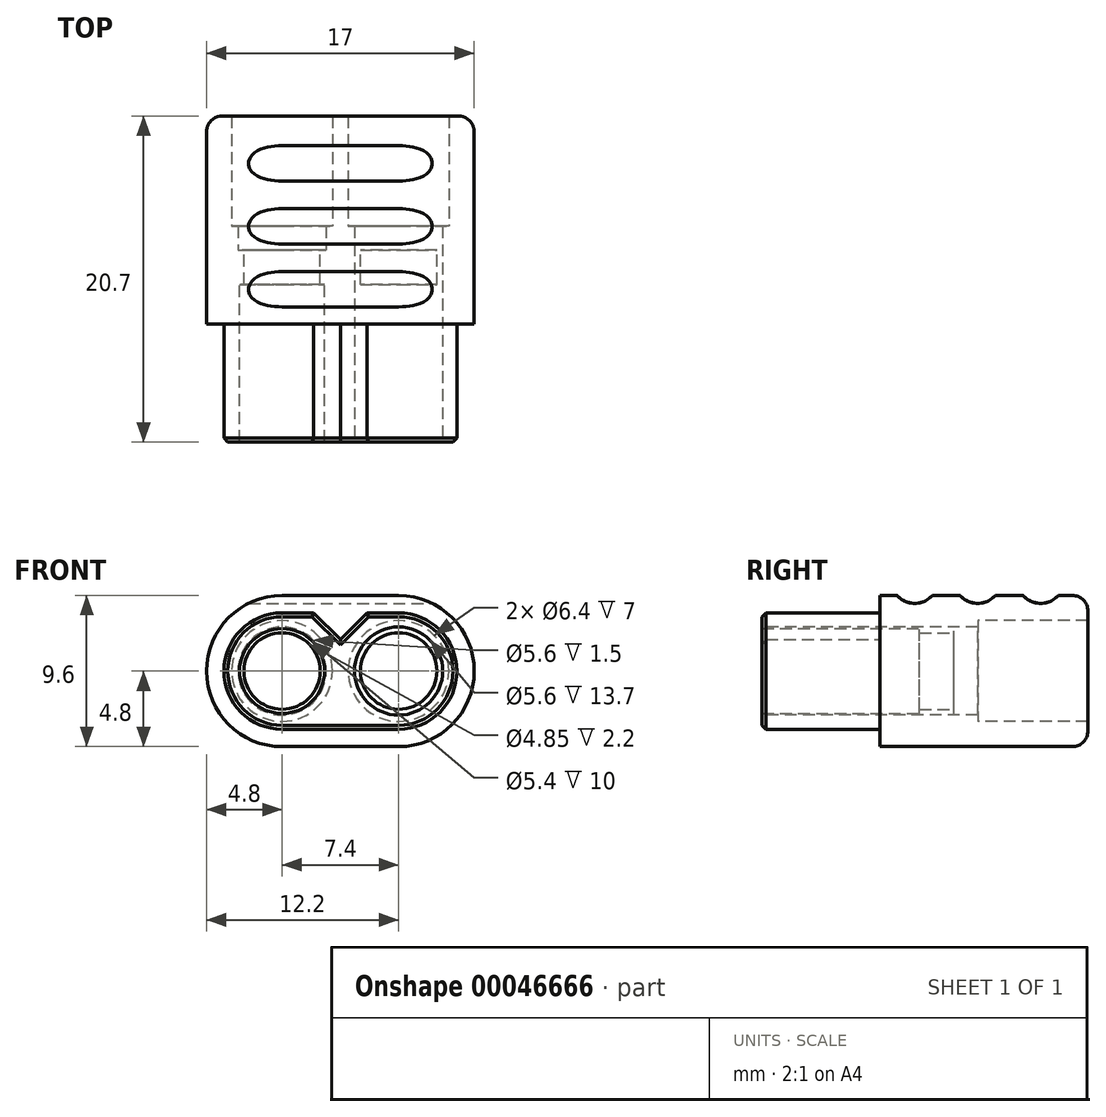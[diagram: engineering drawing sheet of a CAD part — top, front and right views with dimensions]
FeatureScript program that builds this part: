
annotation { "Feature Type Name" : "Feature", "Feature Type Description" : "" }
export const myFeature = defineFeature(function(context is Context, id is Id, definition is map)
    precondition{}
    {
        {
            var Q0;
            Q0=qCreatedBy(makeId("Front.planeOp"),FACE);
            var sketch = newSketch(context, id + "F0", { "sketchPlane" : qUnion([Q0])});
            skCircle(sketch, "E0", {"center": v(-3.7, 0) * mm, "radius": 2.43 * mm});
            skCircle(sketch, "E1.MirrorC", {"center": v(-3.7, 0) * mm, "radius": 2.8 * mm});
            skLineSegment(sketch, "E2", {"start": v(0, 0) * mm, "end": v(-8.5, 0) * mm, "construction": true});
            skArc(sketch, "E3", {"start": v(-3.7, 4.8) * mm, "mid": v(-7.1, 3.4) * mm, "end": v(-8.5, 0) * mm});
            skLineSegment(sketch, "E4", {"start": v(0, 4.8) * mm, "end": v(0, 0) * mm, "construction": true});
            skLineSegment(sketch, "E5", {"start": v(-3.7, 4.8) * mm, "end": v(-3.7, 0) * mm, "construction": true});
            skCircle(sketch, "E6.MirrorC", {"center": v(3.7, 0) * mm, "radius": 2.43 * mm});
            skCircle(sketch, "E7.MirrorC", {"center": v(3.7, 0) * mm, "radius": 2.8 * mm});
            skLineSegment(sketch, "E8", {"start": v(-3.7, 4.8) * mm, "end": v(0, 4.8) * mm});
            skArc(sketch, "E9.MirrorCS", {"start": v(-3.7, -4.8) * mm, "mid": v(-7.1, -3.4) * mm, "end": v(-8.5, 0) * mm});
            skLineSegment(sketch, "E10.MirrorCS", {"start": v(-3.7, -4.8) * mm, "end": v(0, -4.8) * mm});
            skLineSegment(sketch, "E11.MirrorCS", {"start": v(3.7, 4.8) * mm, "end": v(0, 4.8) * mm});
            skArc(sketch, "E12.MirrorCS", {"start": v(3.7, 4.8) * mm, "mid": v(7.1, 3.4) * mm, "end": v(8.5, 0) * mm});
            skArc(sketch, "E13.MirrorCS", {"start": v(3.7, -4.8) * mm, "mid": v(7.1, -3.4) * mm, "end": v(8.5, 0) * mm});
            skLineSegment(sketch, "E14.MirrorCS", {"start": v(3.7, -4.8) * mm, "end": v(0, -4.8) * mm});
            skSolve(sketch);
        }
        {
            var Q0;
            Q0=makeQuery(id+"F0.imprint","IMPRINT",FACE,{"disambiguationData":[TD([[makeQuery(id+"F0.imprint","IMPRINT",EDGE,{"derivedFrom":sQuery(id+"F0.wireOp",EDGE,"E1.MirrorC")}),-1.0]])]});
            extrude(context, id + "F1", {"entities" : qUnion([Q0]), "oppositeDirection" : true, "depth" : 1.5 * mm});
        }
        {
            var Q0;
            Q0=makeQuery(id+"F0.imprint","IMPRINT",FACE,{"disambiguationData":[TD([[makeQuery(id+"F0.imprint","IMPRINT",EDGE,{"derivedFrom":sQuery(id+"F0.wireOp",EDGE,"E1.MirrorC")}),-1.0]])]});
            var Q1;
            Q1=makeQuery(id+"F0.imprint","IMPRINT",FACE,{"disambiguationData":[TD([[makeQuery(id+"F0.imprint","IMPRINT",EDGE,{"derivedFrom":sQuery(id+"F0.wireOp",EDGE,"E0")}),-1.0]])]});
            var Q2;
            Q2=makeQuery(id+"F0.imprint","IMPRINT",FACE,{"disambiguationData":[TD([[makeQuery(id+"F0.imprint","IMPRINT",EDGE,{"derivedFrom":sQuery(id+"F0.wireOp",EDGE,"E6.MirrorC")}),1.0]])]});
            extrude(context, id + "F2", {"entities" : qUnion([Q0, Q1, Q2]), "operationType" : NewBodyOperationType.ADD, "depth" : 2.2 * mm});
        }
        {
            var Q0;
            Q0=makeQuery(id+"F2.opExtrude","CAP_FACE",FACE,{"disambiguationData":[OSD([sQuery(id+"F0.wireOp",EDGE,"9af29b95-2ce9-48ef-83fd-eb93086e848a.bottom"),sQuery(id+"F0.wireOp",EDGE,"9af29b95-2ce9-48ef-83fd-eb93086e848a.top"),sQuery(id+"F0.wireOp",EDGE,"9af29b95-2ce9-48ef-83fd-eb93086e848a.left"),sQuery(id+"F0.wireOp",EDGE,"9af29b95-2ce9-48ef-83fd-eb93086e848a.right"),sQuery(id+"F0.wireOp",EDGE,"E0"),sQuery(id+"F0.wireOp",EDGE,"3bfeefd6-8ccf-4d28-93f8-2f2611132b7e0.MirrorC")])],"isStart":false});
            var sketch = newSketch(context, id + "F3", { "sketchPlane" : qUnion([Q0])});
            skCircle(sketch, "E15", {"center": v(-3.7, 0) * mm, "radius": 2.7 * mm});
            skCircle(sketch, "E16.MirrorC", {"center": v(3.7, 0) * mm, "radius": 2.7 * mm});
            skSolve(sketch);
        }
        {
            var Q0;
            Q0=makeQuery(id+"F3.imprint","IMPRINT",FACE,{"disambiguationData":[TD([[makeQuery(id+"F3.imprint","IMPRINT",EDGE,{"derivedFrom":sQuery(id+"F3.wireOp",EDGE,"E15")}),-1.0]])]});
            extrude(context, id + "F4", {"entities" : qUnion([Q0]), "operationType" : NewBodyOperationType.ADD, "depth" : 2.5 * mm});
        }
        {
            var Q0;
            Q0=makeQuery(id+"F4.opExtrude","CAP_FACE",FACE,{"disambiguationData":[OSD([sQuery(id+"F0.wireOp",EDGE,"6d7ef5f6-68e2-491c-bdb9-d34946de3217"),sQuery(id+"F0.wireOp",EDGE,"4a62e17a-e464-4ae6-85fd-e67879230d62"),sQuery(id+"F0.wireOp",EDGE,"d8da9cf0-fa24-4876-8edd-ab64fd6ac28d"),sQuery(id+"F0.wireOp",EDGE,"6ed2982d-5885-44c9-aeb3-c63c06cbabe1.filletArc"),sQuery(id+"F0.wireOp",EDGE,"ac0d3ca8-c71e-4b4c-905e-2867e2134c0f.filletArc"),sQuery(id+"F0.wireOp",EDGE,"db059e13-4987-40d7-b22c-4aa99c86301e0.MirrorCS"),sQuery(id+"F0.wireOp",EDGE,"21968229-6fcb-4818-9fba-464d6f3a7a490.MirrorCS"),sQuery(id+"F0.wireOp",EDGE,"27c3a9c7-bba5-4ce6-a0b2-ee3fde2fc81d0.MirrorCS"),sQuery(id+"F0.wireOp",EDGE,"74e78b0a-03c2-4682-ad69-f2b08288fff30.MirrorCS"),sQuery(id+"F0.wireOp",EDGE,"d6014dcf-48b1-47f5-9b02-8fcda7855cd30.MirrorCS"),sQuery(id+"F3.wireOp",EDGE,"E15"),sQuery(id+"F3.wireOp",EDGE,"3893830b-eff6-4bac-9637-d990255e7b810.MirrorC")])],"isStart":false});
            var sketch = newSketch(context, id + "F5", { "sketchPlane" : qUnion([Q0])});
            skLineSegment(sketch, "E17", {"start": v(-3.7, -3.7) * mm, "end": v(0, -3.7) * mm});
            skLineSegment(sketch, "E18", {"start": v(-1.7, 3.7) * mm, "end": v(0, 2) * mm});
            skArc(sketch, "E19", {"start": v(-3.7, 3.7) * mm, "mid": v(-7.4, 0) * mm, "end": v(-3.7, -3.7) * mm});
            skLineSegment(sketch, "E20", {"start": v(-3.7, 3.7) * mm, "end": v(-1.7, 3.7) * mm});
            skLineSegment(sketch, "E21.MirrorCS", {"start": v(1.7, 3.7) * mm, "end": v(0, 2) * mm});
            skLineSegment(sketch, "E22.MirrorCS", {"start": v(3.7, 3.7) * mm, "end": v(1.7, 3.7) * mm});
            skArc(sketch, "E23.MirrorCS", {"start": v(3.7, 3.7) * mm, "mid": v(7.4, 0) * mm, "end": v(3.7, -3.7) * mm});
            skLineSegment(sketch, "E24.MirrorCS", {"start": v(3.7, -3.7) * mm, "end": v(0, -3.7) * mm});
            skSolve(sketch);
        }
        {
            var Q0;
            Q0=makeQuery(id+"F5.imprint","IMPRINT",FACE,{"disambiguationData":[TD([[makeQuery(id+"F5.imprint","IMPRINT",EDGE,{"derivedFrom":sQuery(id+"F5.wireOp",EDGE,"dbc5b547-12d9-4310-99b7-08f169881b62")}),1.0]])]});
            var Q1;
            Q1=makeQuery(id+"F5.imprint","IMPRINT",FACE,{"disambiguationData":[TD([[makeQuery(id+"F5.imprint","IMPRINT",EDGE,{"derivedFrom":sQuery(id+"F5.wireOp",EDGE,"E17")}),1.0]])]});
            extrude(context, id + "F6", {"entities" : qUnion([Q0, Q1]), "operationType" : NewBodyOperationType.ADD, "depth" : 7.5 * mm});
        }
        {
            var Q0;
            Q0=makeQuery(id+"F1.opExtrude","CAP_FACE",FACE,{"disambiguationData":[OSD([sQuery(id+"F0.wireOp",EDGE,"E1.MirrorC"),sQuery(id+"F0.wireOp",EDGE,"E3"),sQuery(id+"F0.wireOp",EDGE,"E7.MirrorC"),sQuery(id+"F0.wireOp",EDGE,"E8"),sQuery(id+"F0.wireOp",EDGE,"E9.MirrorCS"),sQuery(id+"F0.wireOp",EDGE,"E10.MirrorCS"),sQuery(id+"F0.wireOp",EDGE,"E11.MirrorCS"),sQuery(id+"F0.wireOp",EDGE,"E12.MirrorCS"),sQuery(id+"F0.wireOp",EDGE,"E13.MirrorCS"),sQuery(id+"F0.wireOp",EDGE,"E14.MirrorCS")])],"isStart":false});
            var sketch = newSketch(context, id + "F7", { "sketchPlane" : qUnion([Q0])});
            skCircle(sketch, "E25", {"center": v(3.7, 0) * mm, "radius": 3.2 * mm});
            skCircle(sketch, "E26.MirrorC", {"center": v(-3.7, 0) * mm, "radius": 3.2 * mm});
            skSolve(sketch);
        }
        {
            var Q0;
            Q0=makeQuery(id+"F7.imprint","IMPRINT",FACE,{"disambiguationData":[TD([[makeQuery(id+"F7.imprint","IMPRINT",EDGE,{"derivedFrom":sQuery(id+"F7.wireOp",EDGE,"E25")}),-1.0]])]});
            extrude(context, id + "F8", {"entities" : qUnion([Q0]), "operationType" : NewBodyOperationType.ADD, "depth" : 7 * mm});
        }
        {
            var Q0;
            Q0=makeQuery(id+"F8.opExtrude","CAP_EDGE",EDGE,{"disambiguationData":[OSD([sQuery(id+"F0.wireOp",EDGE,"E8"),sQuery(id+"F0.wireOp",EDGE,"E11.MirrorCS")])],"isStart":false});
            fillet(context, id + "F9", {"entities" : qUnion([Q0]), "radius" : 1 * mm, "tangentPropagation" : true, "allowEdgeOverflow" : false});
        }
        {
            var Q0;
            Q0=makeQuery(id+"F6.opExtrude","CAP_EDGE",EDGE,{"disambiguationData":[OSD([sQuery(id+"F5.wireOp",EDGE,"E20")])],"isStart":false});
            var Q1;
            Q1=makeQuery(id+"F6.opExtrude","CAP_EDGE",EDGE,{"disambiguationData":[OSD([sQuery(id+"F5.wireOp",EDGE,"E18")])],"isStart":false});
            var Q2;
            Q2=makeQuery(id+"F6.opExtrude","CAP_EDGE",EDGE,{"disambiguationData":[OSD([sQuery(id+"F5.wireOp",EDGE,"E21.MirrorCS")])],"isStart":false});
            chamfer(context, id + "F10", {"entities" : qUnion([Q0, Q1, Q2]), "width" : 0.25 * mm, "tangentPropagation" : true});
        }
        {
            var Q0;
            Q0=qCreatedBy(makeId("Right.planeOp"),FACE);
            var sketch = newSketch(context, id + "F11", { "sketchPlane" : qUnion([Q0])});
            skCircle(sketch, "E27", {"center": v(-2.5, 5.8) * mm, "radius": 1.5 * mm});
            skCircle(sketch, "E28", {"center": v(5.5, 5.8) * mm, "radius": 1.5 * mm});
            skLineSegment(sketch, "E29", {"start": v(9.5, 0) * mm, "end": v(-15.5, 0) * mm, "construction": true});
            skLineSegment(sketch, "E30", {"start": v(5.5, 5.8) * mm, "end": v(-2.5, 5.8) * mm, "construction": true});
            skCircle(sketch, "E31", {"center": v(1.5, 5.8) * mm, "radius": 1.5 * mm});
            skCircle(sketch, "E32.MirrorC", {"center": v(-2.5, -5.8) * mm, "radius": 1.5 * mm});
            skCircle(sketch, "E33.MirrorC", {"center": v(1.5, -5.8) * mm, "radius": 1.5 * mm});
            skCircle(sketch, "E34.MirrorC", {"center": v(5.5, -5.8) * mm, "radius": 1.5 * mm});
            skSolve(sketch);
        }
        {
            var Q0;
            Q0=makeQuery(id+"F11.imprint","IMPRINT",FACE,{"disambiguationData":[TD([[makeQuery(id+"F11.imprint","IMPRINT",EDGE,{"derivedFrom":sQuery(id+"F11.wireOp",EDGE,"E31")}),1.0]])]});
            var Q1;
            Q1=makeQuery(id+"F11.imprint","IMPRINT",FACE,{"disambiguationData":[TD([[makeQuery(id+"F11.imprint","IMPRINT",EDGE,{"derivedFrom":sQuery(id+"F11.wireOp",EDGE,"E27")}),1.0]])]});
            var Q2;
            Q2=makeQuery(id+"F11.imprint","IMPRINT",FACE,{"disambiguationData":[TD([[makeQuery(id+"F11.imprint","IMPRINT",EDGE,{"derivedFrom":sQuery(id+"F11.wireOp",EDGE,"E32.MirrorC")}),-1.0]])]});
            var Q3;
            Q3=makeQuery(id+"F11.imprint","IMPRINT",FACE,{"disambiguationData":[TD([[makeQuery(id+"F11.imprint","IMPRINT",EDGE,{"derivedFrom":sQuery(id+"F11.wireOp",EDGE,"E33.MirrorC")}),-1.0]])]});
            var Q4;
            Q4=makeQuery(id+"F11.imprint","IMPRINT",FACE,{"disambiguationData":[TD([[makeQuery(id+"F11.imprint","IMPRINT",EDGE,{"derivedFrom":sQuery(id+"F11.wireOp",EDGE,"E34.MirrorC")}),-1.0]])]});
            var Q5;
            Q5=makeQuery(id+"F11.imprint","IMPRINT",FACE,{"disambiguationData":[TD([[makeQuery(id+"F11.imprint","IMPRINT",EDGE,{"derivedFrom":sQuery(id+"F11.wireOp",EDGE,"E28")}),1.0]])]});
            extrude(context, id + "F12", {"entities" : qUnion([Q0, Q1, Q2, Q3, Q4, Q5]), "operationType" : NewBodyOperationType.REMOVE, "endBound" : BoundingType.SYMMETRIC, "oppositeDirection" : true, "depth" : 17 * mm});
        }
    });
